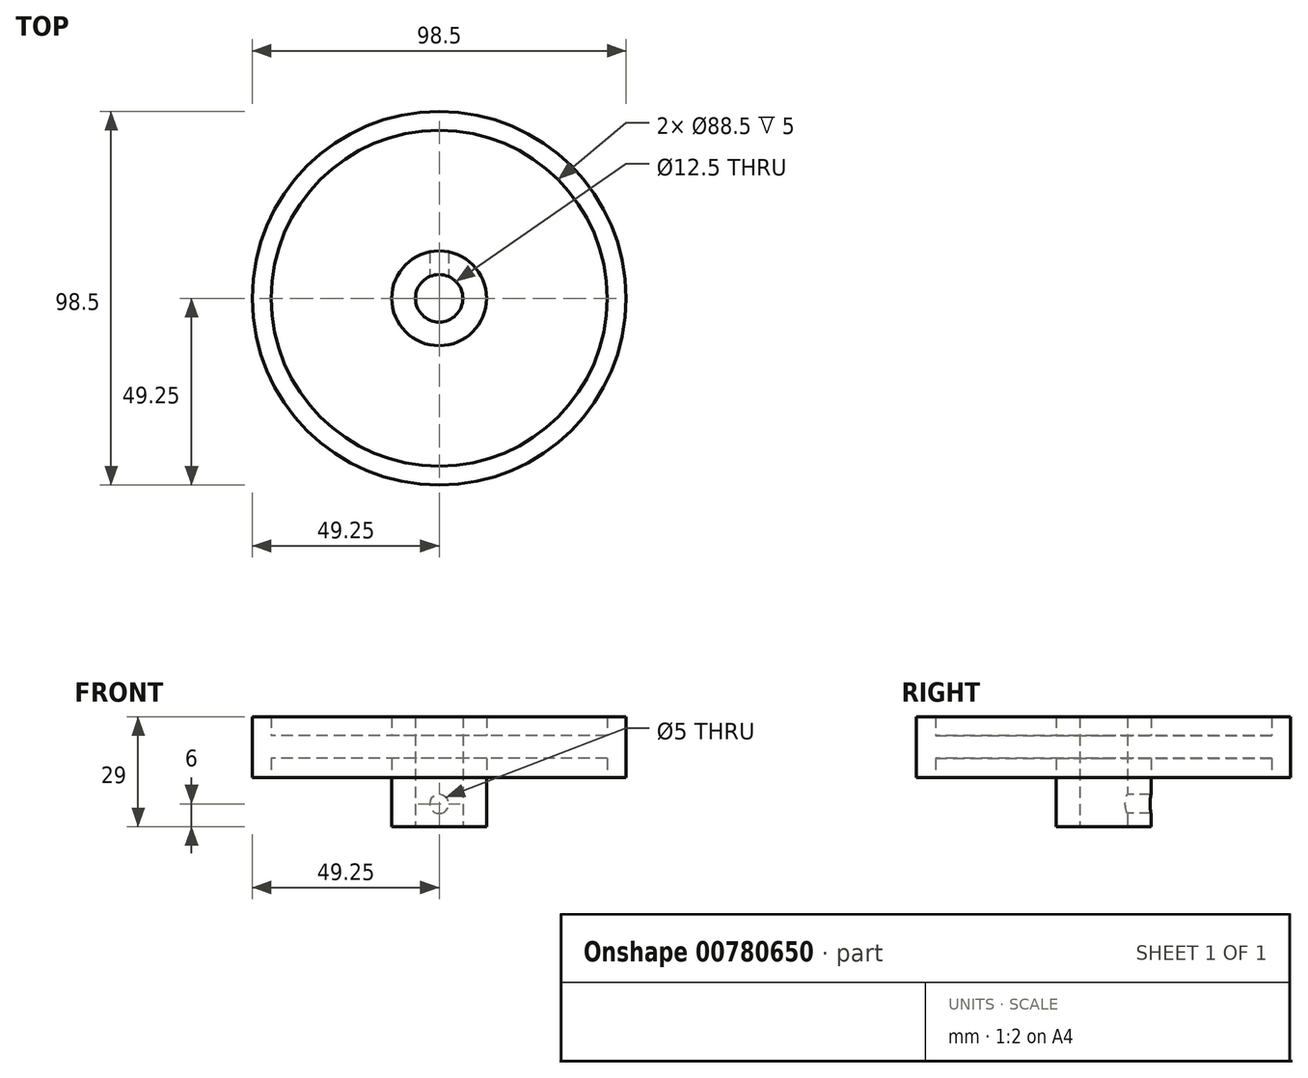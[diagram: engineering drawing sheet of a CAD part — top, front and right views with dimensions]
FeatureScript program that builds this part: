
annotation { "Feature Type Name" : "Feature", "Feature Type Description" : "" }
export const myFeature = defineFeature(function(context is Context, id is Id, definition is map)
    precondition{}
    {
        {
            var Q0;
            Q0=qCreatedBy(makeId("Top.planeOp"),FACE);
            var sketch = newSketch(context, id + "F0", { "sketchPlane" : qUnion([Q0])});
            skCircle(sketch, "E0", {"center": v(0, 0) * mm, "radius": 6.25 * mm});
            skCircle(sketch, "E1", {"center": v(0, 0) * mm, "radius": 12.5 * mm});
            skCircle(sketch, "E2", {"center": v(0, 0) * mm, "radius": 44.25 * mm});
            skCircle(sketch, "E3", {"center": v(0, 0) * mm, "radius": 49.25 * mm});
            skSolve(sketch);
        }
        {
            var Q0;
            Q0=makeQuery(id+"F0.imprint","IMPRINT",FACE,{"disambiguationData":[TD([[makeQuery(id+"F0.imprint","IMPRINT",EDGE,{"derivedFrom":sQuery(id+"F0.wireOp",EDGE,"E2")}),-1.0]])]});
            extrude(context, id + "F1", {"entities" : qUnion([Q0]), "endBound" : BoundingType.SYMMETRIC, "depth" : 16 * mm, "offsetDistance" : 25 * mm});
        }
        {
            var Q0;
            Q0=makeQuery(id+"F0.imprint","IMPRINT",FACE,{"disambiguationData":[TD([[makeQuery(id+"F0.imprint","IMPRINT",EDGE,{"derivedFrom":sQuery(id+"F0.wireOp",EDGE,"E1")}),-1.0]])]});
            extrude(context, id + "F2", {"entities" : qUnion([Q0]), "operationType" : NewBodyOperationType.ADD, "endBound" : BoundingType.SYMMETRIC, "depth" : 6 * mm, "offsetDistance" : 25 * mm});
        }
        {
            var Q0;
            Q0=makeQuery(id+"F0.imprint","IMPRINT",FACE,{"disambiguationData":[TD([[makeQuery(id+"F0.imprint","IMPRINT",EDGE,{"derivedFrom":sQuery(id+"F0.wireOp",EDGE,"E0")}),-1.0]])]});
            extrude(context, id + "F3", {"entities" : qUnion([Q0]), "operationType" : NewBodyOperationType.ADD, "depth" : 8 * mm, "offsetDistance" : 25 * mm, "hasSecondDirection" : true, "secondDirectionOppositeDirection" : true, "secondDirectionDepth" : 21 * mm});
        }
        {
            var Q0;
            Q0=qCreatedBy(makeId("Front.planeOp"),FACE);
            var sketch = newSketch(context, id + "F4", { "sketchPlane" : qUnion([Q0])});
            skLineSegment(sketch, "E4", {"start": v(0, 0) * mm, "end": v(0, -15) * mm});
            skCircle(sketch, "E5", {"center": v(0, -15) * mm, "radius": 2.5 * mm});
            skSolve(sketch);
        }
        {
            var Q0;
            Q0 = qSketchRegion(id + "F4", true);
            extrude(context, id + "F5", {"entities" : qUnion([Q0]), "operationType" : NewBodyOperationType.REMOVE, "oppositeDirection" : true, "depth" : 25 * mm, "offsetDistance" : 25 * mm});
        }
    });
